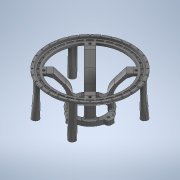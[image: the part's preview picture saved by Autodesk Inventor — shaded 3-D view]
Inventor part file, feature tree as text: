
AUTODESK INVENTOR PART (.ipt)
format: ipt  version: 2020 (Build 240168000, 168)  size: 3,276,800 bytes
history: native  units: mm
features: projected_geometry x28, other x27, sketch x23, extrude x13, fillet x10, revolve x9, pattern_circular x6, loft x6, mirror x5, chamfer x2
ambient origin geometry x8: Origin, YZ Plane, XZ Plane, XY Plane, X Axis, Y Axis, Z Axis, Center Point
bodies: Body1 (feature_tree)
feature tree (129):
  other  "Твердое тело1"
  extrude  "Выдавливание1"  Depth=34.0mm
  other  "РабПлоскость1"
  other  "РабОсь1"
  revolve  "Вращение1"
  extrude  "Выдавливание2"  Depth=45.0mm
  other  "РабТочка2"
  other  "РабТочка3"
  other  "РабТочка4"
  other  "РабПлоскость2"
  sketch  "Эскиз5"
  revolve  "Вращение2"
  revolve  "Вращение3"
  pattern_circular  "Круговой массив1"  Angle=45.0deg  [1 undecoded]
  extrude  "Выдавливание3"  Depth=2.9mm
  revolve  "Вращение4"
  fillet  "Сопряжение1"  Radius=9.0mm
  revolve  "Вращение5"
  other  "РабПлоскость6"
  other  "РабПлоскость7"
  sketch  "Эскиз10"
  revolve  "Вращение6"
  revolve  "Вращение7"
  sketch  "Эскиз11"
  sketch  "Эскиз12"
  loft  "Лофт2"
  loft  "Лофт3"
  fillet  "Сопряжение2"  Radius=1.0mm
  extrude  "Выдавливание4"  Depth=22.0mm
  loft  "Лофт4"
  fillet  "Сопряжение3"  Radius=5.0mm
  pattern_circular  "Круговой массив2"  [2 undecoded]
  revolve  "Вращение8"
  revolve  "Вращение9"
  extrude  "Выдавливание5"  Depth=2.5mm
  extrude  "Выдавливание6"  Depth=45.0mm
  pattern_circular  "Круговой массив3"  [2 undecoded]
  other  "РабПлоскость8"
  extrude  "Выдавливание8"  Depth=2.0mm
  extrude  "Выдавливание7"  Depth=2.0mm
  loft  "Лофт5"
  pattern_circular  "Круговой массив4"  Angle=45.0deg  [1 undecoded]
  fillet  "Сопряжение4"  [1 undecoded]
  chamfer  "Фаска1"  Distance=3.0mm
  sketch  "Эскиз23"
  extrude  "Выдавливание9"  TaperAngle=135.0deg  [1 undecoded]
  loft  "Лофт6"
  other  "РабПлоскость9"
  mirror  "Зеркальное отражение1"
  pattern_circular  "Круговой массив5"  [2 undecoded]
  extrude  "Выдавливание10"  TaperAngle=0.0deg  [1 undecoded]
  pattern_circular  "Круговой массив6"  [2 undecoded]
  other  "board plane"
  sketch  "Эскиз26"
  extrude  "Выдавливание11"  Depth=10.0mm
  extrude  "Выдавливание12"  Depth=2.0mm
  other  "РабПлоскость11"
  sketch  "Эскиз28"
  other  "РабПлоскость12"
  loft  "Лофт9"
  fillet  "Сопряжение5"  [1 undecoded]
  other  "РабПлоскость13"
  extrude  "Выдавливание13"  Depth=2.5mm
  chamfer  "Фаска2"  Angle=90.0deg  [1 undecoded]
  other  "РабПлоскость14"
  mirror  "Зеркальное отражение4"
  mirror  "Зеркальное отражение5"
  fillet  "Сопряжение6"  [1 undecoded]
  other  "РабПлоскость15"
  mirror  "Зеркальное отражение6"
  mirror  "Зеркальное отражение7"
  fillet  "Сопряжение8"  Radius=40.0mm
  fillet  "Сопряжение9"  Radius=78.0mm
  fillet  "Сопряжение10"  [1 undecoded]
  fillet  "Сопряжение11"  Radius=2.9mm
  sketch  "Эскиз1"
  sketch  "Эскиз2"
  sketch  "Эскиз4"
  projected_geometry  "Спроецированная петля1"
  projected_geometry  "Спроецированная петля2"
  projected_geometry  "Спроецированная петля3"
  other  "РабПлоскость3"
  other  "РабПлоскость4"
  other  "РабПлоскость5"
  sketch  "Эскиз6"
  sketch  "Эскиз7"
  sketch  "Эскиз9"
  projected_geometry  "Спроецированная петля4"
  projected_geometry  "Спроецированная петля5"
  other  "Ребра2"
  other  "Ребра3"
  sketch  "Эскиз13"
  projected_geometry  "Спроецированная петля6"
  projected_geometry  "Спроецированная петля7"
  sketch  "Эскиз14"
  projected_geometry  "Спроецированная петля8"
  projected_geometry  "Спроецированная петля9"
  projected_geometry  "Спроецированная петля10"
  sketch  "Эскиз16"
  sketch  "Эскиз17"
  projected_geometry  "Спроецированная петля12"
  projected_geometry  "Спроецированная петля13"
  sketch  "Эскиз18"
  sketch  "Эскиз19"
  projected_geometry  "Спроецированная петля14"
  projected_geometry  "Спроецированная петля15"
  other  "Ребра5"
  sketch  "Эскиз22"
  projected_geometry  "Спроецированная петля16"
  projected_geometry  "Спроецированная петля17"
  projected_geometry  "Спроецированная петля18"
  projected_geometry  "Спроецированная петля19"
  projected_geometry  "Спроецированная петля20"
  sketch  "Эскиз24"
  other  "Ребра6"
  sketch  "Эскиз25"
  projected_geometry  "Спроецированная петля21"
  projected_geometry  "Спроецированная петля22"
  projected_geometry  "Спроецированная петля23"
  projected_geometry  "Спроецированная петля24"
  projected_geometry  "Спроецированная петля27"
  projected_geometry  "Спроецированная петля28"
  projected_geometry  "Спроецированная петля29"
  projected_geometry  "Спроецированная петля30"
  sketch  "Эскиз29"
  other  "Ребра15"
  projected_geometry  "Спроецированная петля31"
  other  "Ребра16"
  other  "Ребра17"
note: 17 required parameter values undecoded (feature->parameter linkage not recoverable at this tier; creation-order binding heuristic only, values carry confidence <= 0.55)
